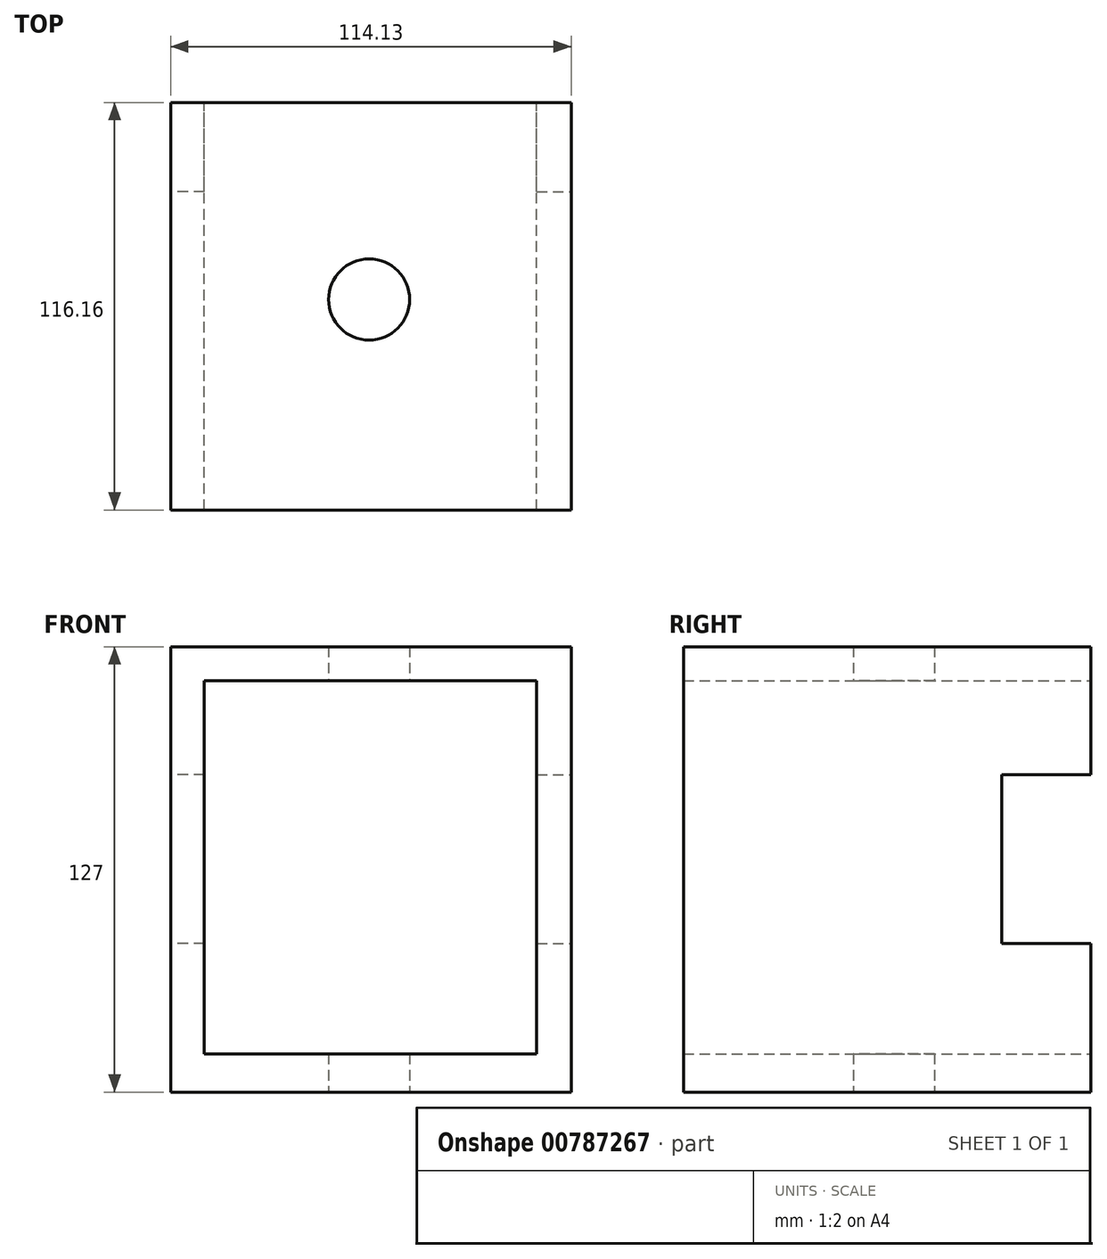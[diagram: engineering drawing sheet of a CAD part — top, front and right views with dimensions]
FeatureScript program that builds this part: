
annotation { "Feature Type Name" : "Feature", "Feature Type Description" : "" }
export const myFeature = defineFeature(function(context is Context, id is Id, definition is map)
    precondition{}
    {
        {
            var Q0;
            Q0=qCreatedBy(makeId("Top.planeOp"),FACE);
            var sketch = newSketch(context, id + "F0", { "sketchPlane" : qUnion([Q0])});
            skLineSegment(sketch, "E0.bottom", {"start": v(-56.56, 56.15) * mm, "end": v(57.57, 56.15) * mm});
            skLineSegment(sketch, "E0.top", {"start": v(-56.56, -60) * mm, "end": v(57.57, -60) * mm});
            skLineSegment(sketch, "E0.left", {"start": v(-56.56, 56.15) * mm, "end": v(-56.56, -60) * mm});
            skLineSegment(sketch, "E0.right", {"start": v(57.57, 56.15) * mm, "end": v(57.57, -60) * mm});
            skCircle(sketch, "E1", {"center": v(0, 0) * mm, "radius": 11.56 * mm});
            skSolve(sketch);
        }
        {
            var Q0;
            Q0=makeQuery(id+"F0.imprint","IMPRINT",FACE,{"disambiguationData":[TD([[makeQuery(id+"F0.imprint","IMPRINT",EDGE,{"derivedFrom":sQuery(id+"F0.wireOp",EDGE,"E0.bottom")}),-1.0]])]});
            extrude(context, id + "F1", {"entities" : qUnion([Q0]), "depth" : 127 * mm, "offsetDistance" : 25.4 * mm});
        }
        {
            var Q0;
            Q0=makeQuery(id+"F1.opExtrude","SWEPT_FACE",FACE,{"disambiguationData":[OSD([sQuery(id+"F0.wireOp",EDGE,"E0.bottom")])]});
            var sketch = newSketch(context, id + "F2", { "sketchPlane" : qUnion([Q0])});
            skLineSegment(sketch, "E2.bottom", {"start": v(-47.79, 117.32) * mm, "end": v(46.98, 117.32) * mm});
            skLineSegment(sketch, "E2.top", {"start": v(-47.79, 10.91) * mm, "end": v(46.98, 10.91) * mm});
            skLineSegment(sketch, "E2.left", {"start": v(-47.79, 117.32) * mm, "end": v(-47.79, 10.91) * mm});
            skLineSegment(sketch, "E2.right", {"start": v(46.98, 117.32) * mm, "end": v(46.98, 10.91) * mm});
            skLineSegment(sketch, "E3", {"start": v(-47.79, 90.52) * mm, "end": v(-57.57, 90.52) * mm});
            skLineSegment(sketch, "E4", {"start": v(-47.79, 42.32) * mm, "end": v(-57.57, 42.32) * mm});
            skLineSegment(sketch, "E5", {"start": v(46.98, 42.32) * mm, "end": v(56.56, 42.32) * mm});
            skLineSegment(sketch, "E6", {"start": v(46.98, 90.52) * mm, "end": v(56.56, 90.52) * mm});
            skSolve(sketch);
        }
        {
            var Q0;
            {var subQ3=sQuery(id+"F2.wireOp",EDGE,"E2.bottom");Q0=makeQuery(id+"F2.imprint","IMPRINT",FACE,{"disambiguationData":[TD([[makeQuery(id+"F2.imprint","IMPRINT",EDGE,{"derivedFrom":subQ3}),-1.0]])]});}
            extrude(context, id + "F3", {"entities" : qUnion([Q0]), "operationType" : NewBodyOperationType.REMOVE, "oppositeDirection" : true, "depth" : 2514.6 * mm, "offsetDistance" : 25.4 * mm});
        }
        {
            var Q0;
            {var subQ0=sQuery(id+"F2.wireOp",EDGE,"E3");Q0=makeQuery(id+"F2.imprint","IMPRINT",FACE,{"disambiguationData":[TD([[makeQuery(id+"F2.imprint","IMPRINT",EDGE,{"derivedFrom":subQ0}),1.0]])]});}
            extrude(context, id + "F4", {"entities" : qUnion([Q0]), "operationType" : NewBodyOperationType.REMOVE, "oppositeDirection" : true, "depth" : 25.4 * mm, "offsetDistance" : 25.4 * mm});
        }
        {
            var Q0;
            {var subQ0=sQuery(id+"F2.wireOp",EDGE,"E5");Q0=makeQuery(id+"F2.imprint","IMPRINT",FACE,{"disambiguationData":[TD([[makeQuery(id+"F2.imprint","IMPRINT",EDGE,{"derivedFrom":subQ0}),1.0]])]});}
            extrude(context, id + "F5", {"entities" : qUnion([Q0]), "operationType" : NewBodyOperationType.REMOVE, "oppositeDirection" : true, "depth" : 25.4 * mm, "offsetDistance" : 25.4 * mm});
        }
    });
